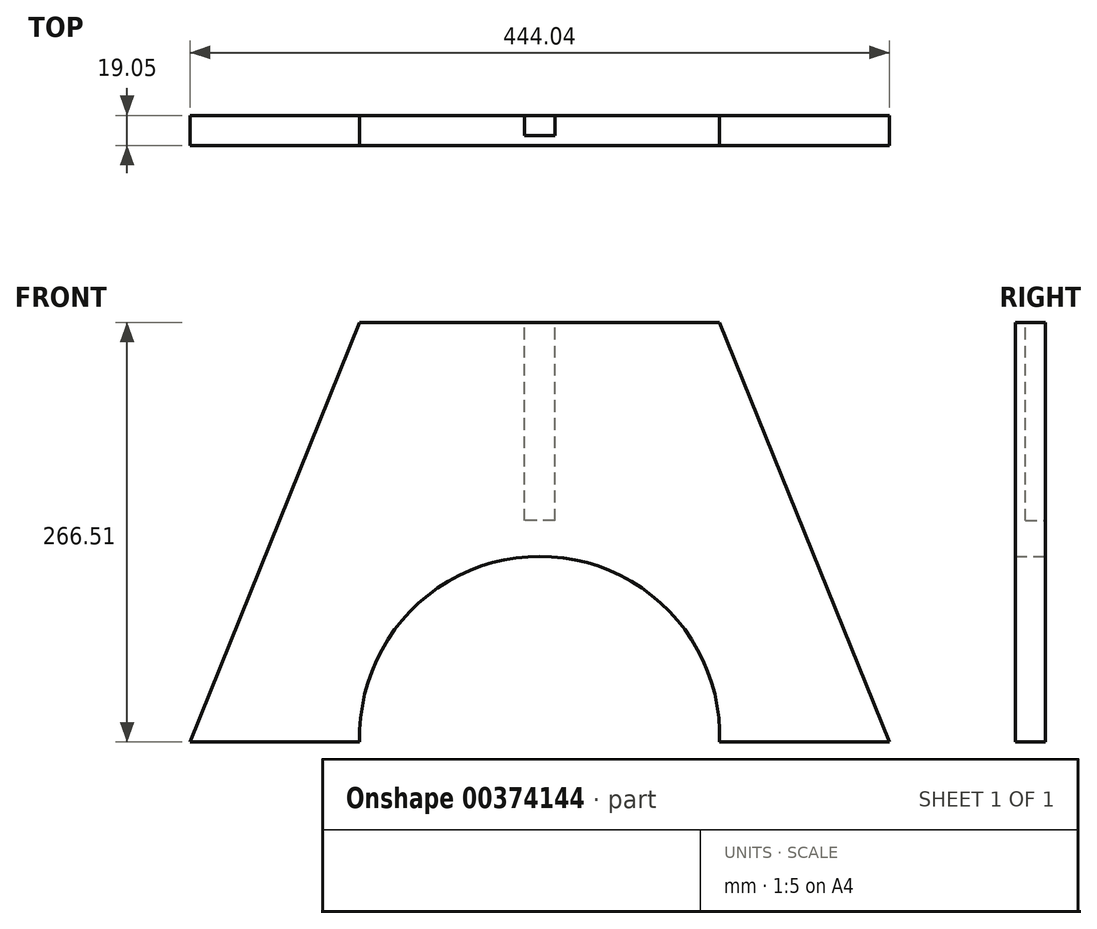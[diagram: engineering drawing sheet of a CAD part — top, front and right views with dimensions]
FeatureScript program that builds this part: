
annotation { "Feature Type Name" : "Feature", "Feature Type Description" : "" }
export const myFeature = defineFeature(function(context is Context, id is Id, definition is map)
    precondition{}
    {
        {
            var Q0;
            Q0=qCreatedBy(makeId("Front.planeOp"),FACE);
            var sketch = newSketch(context, id + "F0", { "sketchPlane" : qUnion([Q0])});
            skLineSegment(sketch, "E0", {"start": v(0, 149.93) * mm, "end": v(114.3, 149.93) * mm});
            skLineSegment(sketch, "E1", {"start": v(0, 149.93) * mm, "end": v(-114.3, 149.93) * mm});
            skLineSegment(sketch, "E2", {"start": v(114.3, 149.93) * mm, "end": v(222.02, -116.58) * mm});
            skLineSegment(sketch, "E3", {"start": v(222.02, -116.58) * mm, "end": v(114.3, -116.58) * mm});
            skLineSegment(sketch, "E4", {"start": v(0, 149.93) * mm, "end": v(0, 1.4) * mm, "construction": true});
            skLineSegment(sketch, "E5.MirrorCS", {"start": v(-114.3, 149.93) * mm, "end": v(-222.02, -116.58) * mm});
            skLineSegment(sketch, "E6.MirrorCS", {"start": v(-222.02, -116.58) * mm, "end": v(-114.3, -116.58) * mm});
            skArc(sketch, "E7", {"start": v(114.3, -116.58) * mm, "mid": v(0, 1.4) * mm, "end": v(-114.3, -116.58) * mm});
            skPoint(sketch, "E7.third.point", {"position": v(-114.3, -109.32) * mm});
            skLineSegment(sketch, "E8.trimOffspring", {"start": v(0, -112.95) * mm, "end": v(0, -115.14) * mm, "construction": true});
            skSolve(sketch);
        }
        {
            var Q0;
            Q0=qSketchRegion(id+"F0",true);
            extrude(context, id + "F1", {"entities" : qUnion([Q0]), "depth" : 19.05 * mm});
        }
        {
            var Q0;
            Q0=qCreatedBy(makeId("Front.planeOp"),FACE);
            var sketch = newSketch(context, id + "F2", { "sketchPlane" : qUnion([Q0])});
            skLineSegment(sketch, "E9", {"start": v(0, 0) * mm, "end": v(0, 24.15) * mm, "construction": true});
            skLineSegment(sketch, "E10", {"start": v(0, 24.15) * mm, "end": v(-9.65, 24.15) * mm});
            skPoint(sketch, "E11.orphan", {"position": v(0, 96.49) * mm});
            skLineSegment(sketch, "E12", {"start": v(0, 24.15) * mm, "end": v(0, 157.41) * mm, "construction": true});
            skLineSegment(sketch, "E13.MirrorCS", {"start": v(0, 24.15) * mm, "end": v(9.65, 24.15) * mm});
            skLineSegment(sketch, "E14", {"start": v(9.65, 24.15) * mm, "end": v(9.65, 151.1) * mm});
            skLineSegment(sketch, "E15", {"start": v(9.65, 151.1) * mm, "end": v(0, 151.1) * mm});
            skLineSegment(sketch, "E16.MirrorCS", {"start": v(-9.65, 24.15) * mm, "end": v(-9.65, 151.1) * mm});
            skLineSegment(sketch, "E17.MirrorCS", {"start": v(-9.65, 151.1) * mm, "end": v(0, 151.1) * mm});
            skSolve(sketch);
        }
        {
            var Q0;
            Q0=qSketchRegion(id+"F2",true);
            extrude(context, id + "F3", {"entities" : qUnion([Q0]), "operationType" : NewBodyOperationType.REMOVE, "depth" : 12.7 * mm});
        }
    });
